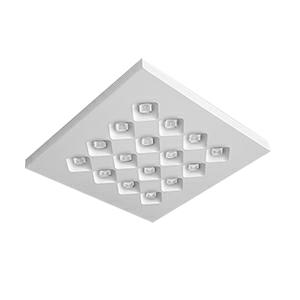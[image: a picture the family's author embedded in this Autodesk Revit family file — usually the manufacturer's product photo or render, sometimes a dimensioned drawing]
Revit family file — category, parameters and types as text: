
# Revit family: 3f_filippi_-_3f_diagon_3f_filippi_-_23027_a0686_-_3f_diagon_39w-840_596x596___corn_plaf__fedc
name_source: partatom
category: Lighting Fixtures
units: mm (PartAtom-declared; Revit-internal decimal feet)

## family parameters
Cut with Voids When Loaded = No
Host = Face
Light Source = No
Part Type = Normal
Room Calculation Point = No
Round Connector Dimension = Use Diameter
Shared = No

## types (1)
- 3F Filippi - 3F Dìagon (1 x LED, 5796 lm, 40 W, 4000 K)
    Apparent Load = 40 VA
    Approval mark = CE
    CIE Flux Codes = 67 96 100 100 100
    Color Rendering = 80
    Color Temperature = 4000 K
    Control Gear = Electronic ballast
    Default Elevation = 1800 mm
    Description = ILLUMINOTECHNICAL
Luminous efficiency 100% (DLOR 100%, ULOR 0%).
Initial luminous flux of the luminaire 5796 lm.
Direct symmetric distribution.
Installation Interdistance Transv.D = 1.39 x hu - Long.D = 1.39 x hu.
Average luminance <3000 cd/m² for radial angles >65°.
Tabular UGR (CIE 117 - 4H-8H; S=0.25H; 70/50/20): RUG 18.4 - 18.4.
Beam angle: 93° - 92°.
Luminous efficacy 145 lm/W.
Lifetime (L90/B10): 30000 h. (tq+25°C)
Lifetime (L85/B10): 50000 h. (tq+25°C)
Lifetime (L80/B20): 80000 h. (tq+25°C)
Lifetime (L70/B20): 100000 h. (tq+25°C)
Sudden decreased luminous flux after 50000 hours: 0% (C0).
Photobiological safety in compliance with IEC/TR 62778: RG0 risk exempt, (IEC 62471).
In compliance with IEC/EN 62722-2-1 - IEC/EN 62717 standards.

SOURCE
Squared LED module 39W/840.
Energy efficiency class (UE 2019/2020 - UE 2019/2015): C.
CIE 13.3 Colour rendering index: CRI >80 (R9 <50%).
IES TM-30 Fidelity Index: Rf = 84 Rg = 95.
CCT nominal colour temperature 4000 K.
Colour initial tolerance (MacAdam): SDCM 3.

MECHANICAL
Housing in hot-galvanised steel, painted in white polyester.
Honeycombed diagonal screen in white anti-glare polycarbonate.
Rhomboidal lenses with differentiated surfaces, etched and prismatic to optimise the orientation of the luminous flux, in transparent methacrylate (PMMA).
Luminaire with limited surface temperature. - D - (EN 60598-2-24)
Dimensions: 600x600 mm, height 40 mm. Weight 6.165 kg.
IP43 protection degree for exposed part, IP20 for recessed part.
Mechanical strength to impacts IK06 (1 joule).
Glow-wire test resistance 650°C.

ELECTRICAL
Halogen Free electronic wiring 230V-50/60Hz, power factor 0.90, THD <25%, constant output current, class I, 1 driver.
Power of the luminaire 40 W.
ENEC - CE.
SAFE FLICKER: PstLM=<1 and SVM=<0.4 (IEC TR 61547-1 and IEC TR 63158), to ensure a more comfortable and safe light.
Luminaire compliant with EN 60598-2-22 for power supply from a centralised emergency system CPSS (Central Power Supply System), not incorporated in the luminaire - high risk areas excluded. The default power and flux are 100% in AC and 100% in DC.
Ambient temperature from 0°C to +25°C.
Temperature class T6 max 85°C.
Quick connection.
Relative humidity UR: <85%.

INSTALLATION
Ceiling.
Height only 40 mm.
All accessories dedicated to this product are available on the Catalog and on our website www.3F-Filippi.com.

ACCESSORIES
A0686 - 596x596 Diagon frame for Ceiling installation.

APPLICATIONS
Environments: staterooms, with VDTs, offices.
Environments with exacting visual tasks, where diffused soft light for optimum visual comfort is required.

WARNING
Luminaire designed for disposal/recycling at end-of-life.
Replaceable (LED only) light source by a professional. Replaceable control gear by a professional.
    Height = 0 mm  [stored 0 ft]
    Lamp = 1 x LED
    Lamp Light Flux = 5796 lm
    Lamp Power = 40 W
    Lamp count = 1
    Length = 600 mm
    Lifetime = 50000 h
    Luminous efficacy = 145 lm/W
    Manufacturer = 3F Filippi
    ModVariant = No
    Model = 3F Filippi - 23027+A0686 - 3F Diagon 39W-840 596x596 + Corn.plaf.
    Mounting Place = Ceiling
    Mounting Type = Recessed
    Number of Poles = 1
    OnlyDefault = Yes
    Power Factor = 1
    Product Name = 3F Filippi - 3F Dìagon
    Product group = recessed luminaire
    ProductGroupID = 4
    Protection Class = Protection class I
    Protection Degree = IP 20
    RLX_Detail_Level = 1
    RLX_Emergency_Light_Flux = 0 lm
    RLX_Emergency_Type = 0
    RLX_Emergency_Type_DB = No
    RlxData = <blob elided: 96261 chars, md5=c4394527>
    Socket = socket
    Standby Power = 0 W
    System Light Flux = 5796 lm
    System Power = 40 W
    Type Comments = Product without accessories
    Type Image = 3ffilippi_3f_diagon__a0686.jpg
    URL = http://relux.com
    VarID = ---
    Voltage = 0 V
    Weight = 0.00 kg
    Width = 600 mm

note: [stored X ft] marks values corroborated as IEEE doubles in the binary element streams (Revit-internal decimal feet)

## geometry (parser evidence)
native form markers: Blend x4, Sweep x10
no freeform markers — native parametric forms only
